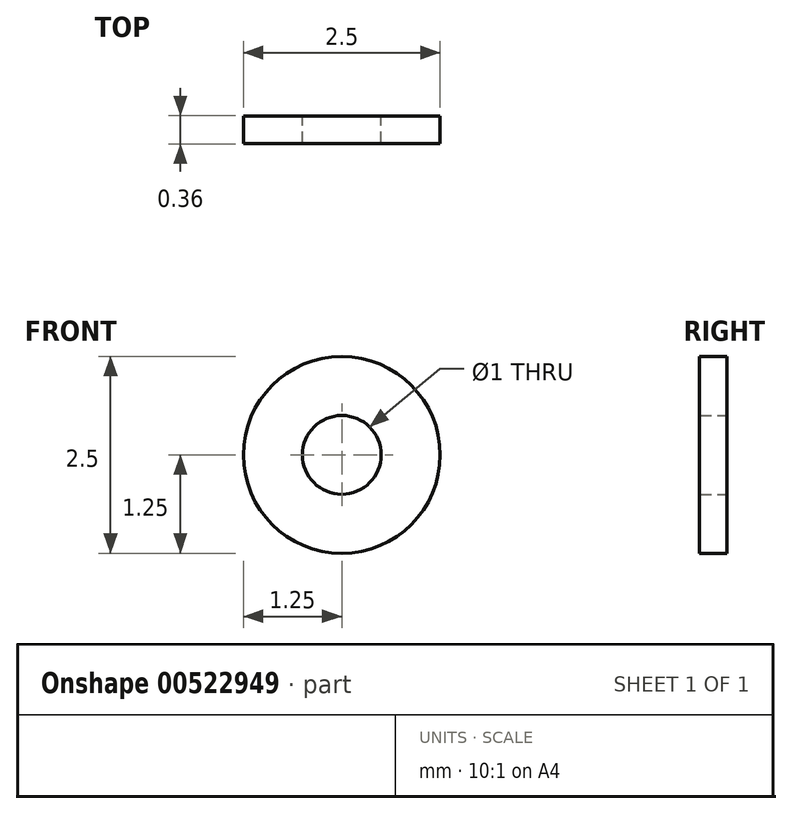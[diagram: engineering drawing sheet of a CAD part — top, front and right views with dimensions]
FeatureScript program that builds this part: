
annotation { "Feature Type Name" : "Feature", "Feature Type Description" : "" }
export const myFeature = defineFeature(function(context is Context, id is Id, definition is map)
    precondition{}
    {
        {
            var Q0;
            Q0=qCreatedBy(makeId("Front.planeOp"),FACE);
            var sketch = newSketch(context, id + "F0", { "sketchPlane" : qUnion([Q0])});
            skCircle(sketch, "E0", {"center": v(0, 3.28) * mm, "radius": 1.25 * mm});
            skCircle(sketch, "E1", {"center": v(0, 3.28) * mm, "radius": 0.5 * mm});
            skSolve(sketch);
        }
        {
            var Q0;
            Q0 = qSketchRegion(id + "F0", true);
            extrude(context, id + "F1", {"entities" : qUnion([Q0]), "endBound" : BoundingType.SYMMETRIC, "depth" : 0.35 * mm, "offsetDistance" : 25 * mm});
        }
    });
